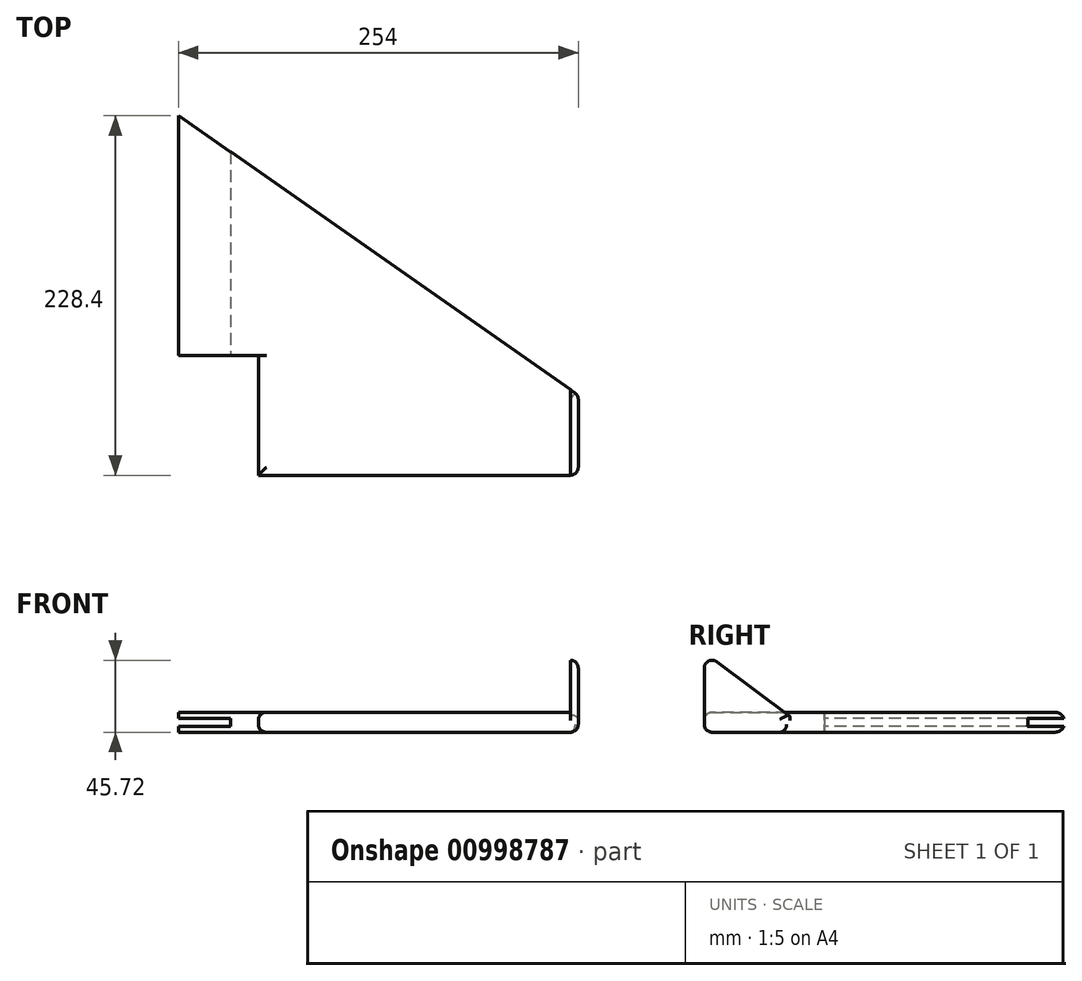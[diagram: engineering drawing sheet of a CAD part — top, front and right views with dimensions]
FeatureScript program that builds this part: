
annotation { "Feature Type Name" : "Feature", "Feature Type Description" : "" }
export const myFeature = defineFeature(function(context is Context, id is Id, definition is map)
    precondition{}
    {
        {
            var Q0;
            Q0=qCreatedBy(makeId("Top.planeOp"),FACE);
            var sketch = newSketch(context, id + "F0", { "sketchPlane" : qUnion([Q0])});
            skLineSegment(sketch, "E0", {"start": v(-173.26, 0) * mm, "end": v(-173.26, 152.4) * mm});
            skLineSegment(sketch, "E1", {"start": v(-173.26, 0) * mm, "end": v(-122.46, 0) * mm});
            skLineSegment(sketch, "E2", {"start": v(-122.46, 0) * mm, "end": v(-122.46, -76.2) * mm});
            skLineSegment(sketch, "E3", {"start": v(-122.46, -76.2) * mm, "end": v(80.74, -76.2) * mm});
            skLineSegment(sketch, "E4", {"start": v(80.74, -76.2) * mm, "end": v(80.74, -25.4) * mm});
            skLineSegment(sketch, "E5", {"start": v(80.74, -25.4) * mm, "end": v(-173.26, 152.4) * mm});
            skSolve(sketch);
        }
        {
            var Q0;
            Q0=makeQuery(id+"F0.imprint","IMPRINT",FACE,{"disambiguationData":[TD([[makeQuery(id+"F0.imprint","IMPRINT",EDGE,{"derivedFrom":sQuery(id+"F0.wireOp",EDGE,"E0")}),-1.0]])]});
            extrude(context, id + "F1", {"entities" : qUnion([Q0]), "depth" : 12.7 * mm, "offsetDistance" : 25.4 * mm});
        }
        {
            var Q0;
            Q0=makeQuery(id+"F1.opExtrude","SWEPT_FACE",FACE,{"disambiguationData":[OSD([sQuery(id+"F0.wireOp",EDGE,"E4")])]});
            var sketch = newSketch(context, id + "F2", { "sketchPlane" : qUnion([Q0])});
            skLineSegment(sketch, "E6", {"start": v(-25.4, 0) * mm, "end": v(-76.2, 0) * mm});
            skLineSegment(sketch, "E7", {"start": v(-76.2, 0) * mm, "end": v(-76.2, 50.8) * mm});
            skPoint(sketch, "E7.endSnap0", {"position": v(-76.2, 6.35) * mm});
            skLineSegment(sketch, "E8", {"start": v(-76.2, 50.8) * mm, "end": v(-25.4, 12.7) * mm});
            skSolve(sketch);
        }
        {
            var Q0;
            {var subQ2=sQuery(id+"F2.wireOp",EDGE,"E8");Q0=makeQuery(id+"F2.imprint","IMPRINT",FACE,{"disambiguationData":[TD([[makeQuery(id+"F2.imprint","IMPRINT",EDGE,{"derivedFrom":subQ2}),-1.0]])]});}
            extrude(context, id + "F3", {"entities" : qUnion([Q0]), "operationType" : NewBodyOperationType.ADD, "oppositeDirection" : true, "depth" : 5.08 * mm, "offsetDistance" : 25.4 * mm});
        }
        {
            var Q0;
            Q0=makeQuery(id+"F1.opExtrude","CAP_EDGE",EDGE,{"disambiguationData":[OSD([sQuery(id+"F0.wireOp",EDGE,"E5")])],"isStart":false});
            var Q1;
            Q1=makeQuery(id+"F1.opExtrude","CAP_EDGE",EDGE,{"disambiguationData":[OSD([sQuery(id+"F0.wireOp",EDGE,"E5")])],"isStart":true});
            var Q2;
            Q2=makeQuery(id+"F1.opExtrude","CAP_EDGE",EDGE,{"disambiguationData":[OSD([sQuery(id+"F0.wireOp",EDGE,"E2")])],"isStart":false});
            var Q3;
            Q3=makeQuery(id+"F1.opExtrude","CAP_EDGE",EDGE,{"disambiguationData":[OSD([sQuery(id+"F0.wireOp",EDGE,"E2")])],"isStart":true});
            var Q4;
            Q4=makeQuery(id+"F1.opExtrude","CAP_EDGE",EDGE,{"disambiguationData":[OSD([sQuery(id+"F0.wireOp",EDGE,"E3")])],"isStart":false});
            var Q5;
            Q5=makeQuery(id+"F1.opExtrude","CAP_EDGE",EDGE,{"disambiguationData":[OSD([sQuery(id+"F0.wireOp",EDGE,"E3")])],"isStart":true});
            fillet(context, id + "F4", {"entities" : qUnion([Q0, Q1, Q2, Q3, Q4, Q5]), "radius" : 5.08 * mm, "tangentPropagation" : true, "allowEdgeOverflow" : false});
        }
        {
            var Q0;
            Q0=makeQuery(id+"F1.opExtrude","SWEPT_FACE",FACE,{"disambiguationData":[OSD([sQuery(id+"F0.wireOp",EDGE,"E1")])]});
            var sketch = newSketch(context, id + "F5", { "sketchPlane" : qUnion([Q0])});
            skLineSegment(sketch, "E9.bottom", {"start": v(-173.26, 8.9) * mm, "end": v(-140.24, 8.9) * mm});
            skLineSegment(sketch, "E9.top", {"start": v(-173.26, 3.81) * mm, "end": v(-140.24, 3.81) * mm});
            skLineSegment(sketch, "E9.left", {"start": v(-173.26, 8.9) * mm, "end": v(-173.26, 3.81) * mm});
            skLineSegment(sketch, "E9.right", {"start": v(-140.24, 8.9) * mm, "end": v(-140.24, 3.81) * mm});
            skSolve(sketch);
        }
        {
            var Q0;
            Q0=makeQuery(id+"F5.imprint","IMPRINT",FACE,{"disambiguationData":[TD([[makeQuery(id+"F5.imprint","IMPRINT",EDGE,{"derivedFrom":sQuery(id+"F5.wireOp",EDGE,"E9.bottom")}),-1.0]])]});
            extrude(context, id + "F6", {"entities" : qUnion([Q0]), "operationType" : NewBodyOperationType.REMOVE, "endBound" : BoundingType.THROUGH_ALL, "oppositeDirection" : true, "depth" : 25.4 * mm, "offsetDistance" : 25.4 * mm});
        }
        {
            var Q0;
            Q0=makeQuery(id+"F3.opExtrude","SWEPT_EDGE",EDGE,{"disambiguationData":[OSD([sQuery(id+"F2.wireOp",EDGE,"E7"),sQuery(id+"F2.wireOp",EDGE,"E8")])]});
            var Q1;
            Q1=makeQuery(id+"F3.opExtrude","CAP_EDGE",EDGE,{"disambiguationData":[OSD([sQuery(id+"F2.wireOp",EDGE,"E8")])],"isStart":true});
            var Q2;
            Q2=makeQuery(id+"F3.boolean.opBoolean","MERGE",EDGE,{"derivedFrom":[makeQuery(id+"F1.opExtrude","SWEPT_EDGE",EDGE,{"disambiguationData":[OSD([sQuery(id+"F0.wireOp",EDGE,"E3"),sQuery(id+"F0.wireOp",EDGE,"E4")])]}),makeQuery(id+"F3.opExtrude","CAP_EDGE",EDGE,{"disambiguationData":[OSD([sQuery(id+"F2.wireOp",EDGE,"E7")])],"isStart":true})]});
            var Q3;
            Q3=makeQuery(id+"F1.opExtrude","CAP_EDGE",EDGE,{"disambiguationData":[OSD([sQuery(id+"F0.wireOp",EDGE,"E4")])],"isStart":true});
            fillet(context, id + "F7", {"entities" : qUnion([Q0, Q1, Q2, Q3]), "radius" : 5.08 * mm, "tangentPropagation" : true, "allowEdgeOverflow" : false});
        }
    });
